# Revit family: 3602A NX PIR High Mount Outdoor Sensor Module_081817
name_source: partatom
category: Communication Devices
units: mm (PartAtom-declared; Revit-internal decimal feet)

## family parameters
Cut with Voids When Loaded = No
Host = Face
Maintain Annotation Orientation = No
OmniClass Number = 23.85.80.11.27
OmniClass Title = Lighting Controls
Part Type = Normal
Room Calculation Point = No
Round Connector Dimension = Use Diameter
Shared = Yes

## types (2) — shared parameters
Assembly Code = D5090
Certifications = Bluetooth Versions 4.1, FCC Part 15.247
Construction = ABS (UL-945VA) flame class rating, UV inhibitors
Coverage = 1:1.4 (mounting height: coverage radius) up to 45’ indoors, 30’ outdoors
Default Elevation = 48 "
Description = The  Control Solutions NXSMP High Mount Sensor
Module provides a unique solution for integrating automatic
control functions directly into a luminaire.
Housing Material = Paint - Matte White
Manufacturer = NX Lighting Controls
Model = NX High Mount Outdoor Sensor Module
Mounting = Mounts in 1.5” diameter aperture, secured by supplied nut on threaded body
Power Requirements = 12VDC, 30 mA supplied by NXFM or NXRC
Sensing Element = Metal-Nickel
Technology = Passive Infrared
Timer Timeout = Automatic mode:1 sec - 20 min
Type Comments = Outdoor Sensor
URL = https://www.currentlighting.com
Warranty = 5-Years Warranty

## type names
- NXSMP-HMO
- NXSMP-HMO-A
type visibility flags (boolean, named after types; folded from table):
- NXSMP-HMO: Yes: (none)
- NXSMP-HMO-A: Yes: NXSMP-HMO-A

## geometry (parser evidence)
native form markers: Sweep x5
no freeform markers — native parametric forms only
